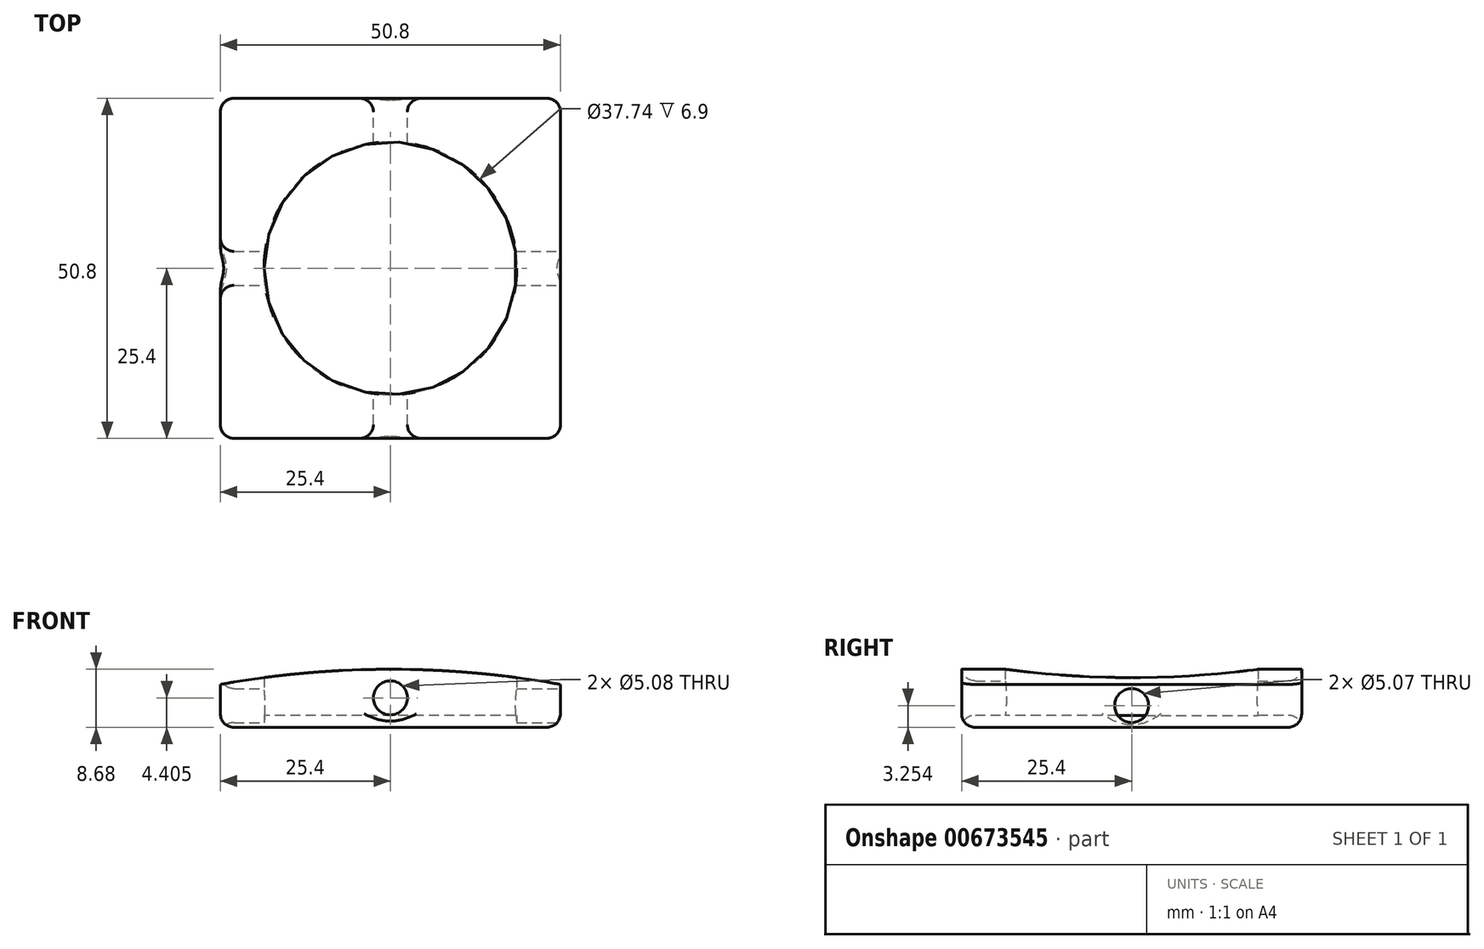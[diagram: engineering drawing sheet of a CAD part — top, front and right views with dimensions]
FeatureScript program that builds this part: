
annotation { "Feature Type Name" : "Feature", "Feature Type Description" : "" }
export const myFeature = defineFeature(function(context is Context, id is Id, definition is map)
    precondition{}
    {
        {
            var Q0;
            Q0=qCreatedBy(makeId("Front.planeOp"),FACE);
            var sketch = newSketch(context, id + "F0", { "sketchPlane" : qUnion([Q0])});
            skCircle(sketch, "E0", {"center": v(0, -120.24) * mm, "radius": 143.51 * mm});
            skLineSegment(sketch, "E1.top", {"start": v(-25.4, 14.6) * mm, "end": v(25.4, 14.6) * mm});
            skLineSegment(sketch, "E1.left", {"start": v(-25.4, 21) * mm, "end": v(-25.4, 14.6) * mm});
            skLineSegment(sketch, "E1.right", {"start": v(25.4, 21) * mm, "end": v(25.4, 14.6) * mm});
            skPoint(sketch, "E1.middle", {"position": v(0, 25.73) * mm});
            skPoint(sketch, "E1.bottom.start.orphan", {"position": v(-25.4, 36.86) * mm});
            skPoint(sketch, "E2.orphan", {"position": v(25.4, 36.86) * mm});
            skCircle(sketch, "E3", {"center": v(0, 19) * mm, "radius": 2.54 * mm});
            skSolve(sketch);
        }
        {
            var Q0;
            Q0=makeQuery(id+"F0.imprint","IMPRINT",FACE,{"disambiguationData":[TD([[makeQuery(id+"F0.imprint","IMPRINT",EDGE,{"derivedFrom":sQuery(id+"F0.wireOp",EDGE,"E1.top")}),1.0]])]});
            extrude(context, id + "F1", {"entities" : qUnion([Q0]), "endBound" : BoundingType.SYMMETRIC, "depth" : 50.8 * mm, "offsetDistance" : 25.4 * mm});
        }
        {
            var Q0;
            Q0=makeQuery(id+"F1.opExtrude","SWEPT_FACE",FACE,{"disambiguationData":[OSD([sQuery(id+"F0.wireOp",EDGE,"E1.right")])]});
            var sketch = newSketch(context, id + "F2", { "sketchPlane" : qUnion([Q0])});
            skCircle(sketch, "E4", {"center": v(0, 17.84) * mm, "radius": 2.54 * mm});
            skSolve(sketch);
        }
        {
            var Q0;
            Q0=makeQuery(id+"F2.imprint","IMPRINT",FACE,{"disambiguationData":[TD([[makeQuery(id+"F2.imprint","IMPRINT",EDGE,{"derivedFrom":sQuery(id+"F2.wireOp",EDGE,"E4")}),1.0]])]});
            extrude(context, id + "F3", {"entities" : qUnion([Q0]), "operationType" : NewBodyOperationType.REMOVE, "oppositeDirection" : true, "depth" : 60.7 * mm, "offsetDistance" : 25.4 * mm});
        }
        {
            var Q0;
            Q0=makeQuery(id+"F1.opExtrude","SWEPT_FACE",FACE,{"disambiguationData":[OSD([sQuery(id+"F0.wireOp",EDGE,"E1.top")])]});
            var sketch = newSketch(context, id + "F4", { "sketchPlane" : qUnion([Q0])});
            skCircle(sketch, "E5", {"center": v(0, 0) * mm, "radius": 18.87 * mm});
            skSolve(sketch);
        }
        {
            var Q0;
            Q0=makeQuery(id+"F4.imprint","IMPRINT",FACE,{"disambiguationData":[TD([[makeQuery(id+"F4.imprint","IMPRINT",EDGE,{"derivedFrom":sQuery(id+"F4.wireOp",EDGE,"E5")}),1.0]])]});
            extrude(context, id + "F5", {"entities" : qUnion([Q0]), "operationType" : NewBodyOperationType.REMOVE, "oppositeDirection" : true, "depth" : 14.48 * mm, "offsetDistance" : 25.4 * mm});
        }
        {
            var Q0;
            Q0=makeQuery(id+"F4.imprint","IMPRINT",FACE,{"disambiguationData":[TD([[makeQuery(id+"F4.imprint","IMPRINT",EDGE,{"derivedFrom":sQuery(id+"F4.wireOp",EDGE,"E5")}),1.0]])]});
            extrude(context, id + "F6", {"entities" : qUnion([Q0]), "operationType" : NewBodyOperationType.ADD, "oppositeDirection" : true, "depth" : 1.78 * mm, "offsetDistance" : 25.4 * mm});
        }
        {
            var Q0;
            Q0=makeQuery(id+"F6.boolean.opBoolean","MERGE",FACE,{"derivedFrom":[makeQuery(id+"F1.opExtrude","SWEPT_FACE",FACE,{"disambiguationData":[OSD([sQuery(id+"F0.wireOp",EDGE,"E1.top")])]}),makeQuery(id+"F6.opExtrude","CAP_FACE",FACE,{"disambiguationData":[OSD([sQuery(id+"F4.wireOp",EDGE,"E5")])],"isStart":true})]});
            var Q1;
            Q1=makeQuery(id+"F1.opExtrude","CAP_EDGE",EDGE,{"disambiguationData":[OSD([sQuery(id+"F0.wireOp",EDGE,"E1.left")])],"isStart":true});
            var Q2;
            Q2=makeQuery(id+"F1.opExtrude","CAP_EDGE",EDGE,{"disambiguationData":[OSD([sQuery(id+"F0.wireOp",EDGE,"E1.left")])],"isStart":false});
            var Q3;
            Q3=makeQuery(id+"F1.opExtrude","CAP_EDGE",EDGE,{"disambiguationData":[OSD([sQuery(id+"F0.wireOp",EDGE,"E1.right")])],"isStart":false});
            var Q4;
            Q4=makeQuery(id+"F1.opExtrude","CAP_EDGE",EDGE,{"disambiguationData":[OSD([sQuery(id+"F0.wireOp",EDGE,"E1.right")])],"isStart":true});
            var Q5;
            Q5=makeQuery(id+"F1.opExtrude","CAP_EDGE",EDGE,{"disambiguationData":[OSD([sQuery(id+"F0.wireOp",EDGE,"E3")])],"isStart":true});
            var Q6;
            Q6=makeQuery(id+"F3.boolean.opBoolean","COPY",EDGE,{"derivedFrom":makeQuery(id+"F3.opExtrude","CAP_EDGE",EDGE,{"disambiguationData":[OSD([sQuery(id+"F2.wireOp",EDGE,"E4")])],"isStart":true})});
            var Q7;
            Q7=makeQuery(id+"F1.opExtrude","CAP_EDGE",EDGE,{"disambiguationData":[OSD([sQuery(id+"F0.wireOp",EDGE,"E3")])],"isStart":false});
            var Q8;
            Q8=makeQuery(id+"F3.boolean.opBoolean","INTERSECT",EDGE,{"derivedFrom":[makeQuery(id+"F1.opExtrude","SWEPT_FACE",FACE,{"disambiguationData":[OSD([sQuery(id+"F0.wireOp",EDGE,"E1.left")])]}),makeQuery(id+"F3.opExtrude","SWEPT_FACE",FACE,{"disambiguationData":[OSD([sQuery(id+"F2.wireOp",EDGE,"E4")])]})]});
            fillet(context, id + "F7", {"entities" : qUnion([Q0, Q1, Q2, Q3, Q4, Q5, Q6, Q7, Q8]), "radius" : 2.03 * mm, "tangentPropagation" : true, "allowEdgeOverflow" : false});
        }
    });
